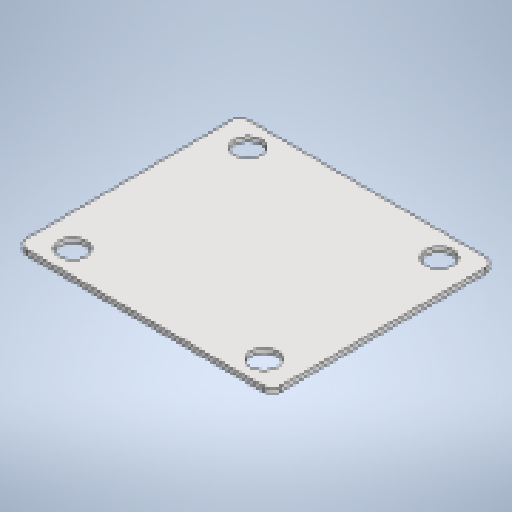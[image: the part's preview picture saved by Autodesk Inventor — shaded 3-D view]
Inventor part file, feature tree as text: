
AUTODESK INVENTOR PART (.ipt)
format: ipt  version: 2025 (Build 290162010, 162A)  size: 168,448 bytes
history: native  units: mm
features: sketch x2, sheet_metal_op x1, chamfer x1, other x1
ambient origin geometry x8: Origin, YZ Plane, XZ Plane, XY Plane, X Axis, Y Axis, Z Axis, Center Point
bodies: Solid1 (feature_tree)
feature tree (5):
  sketch  "3D Sketch1"
  sheet_metal_op  "Face1"
  chamfer  "Corner Round1"
  sketch  "Sketch1"  dims[d0=50.0mm d1=23.865632mm d2=8.726646mm d6=3.0mm d30=140.0mm d34=160.0mm d35=17.0mm d36=20.0mm d37=15.0mm d38=6.0mm]
  other  "Plate1"
